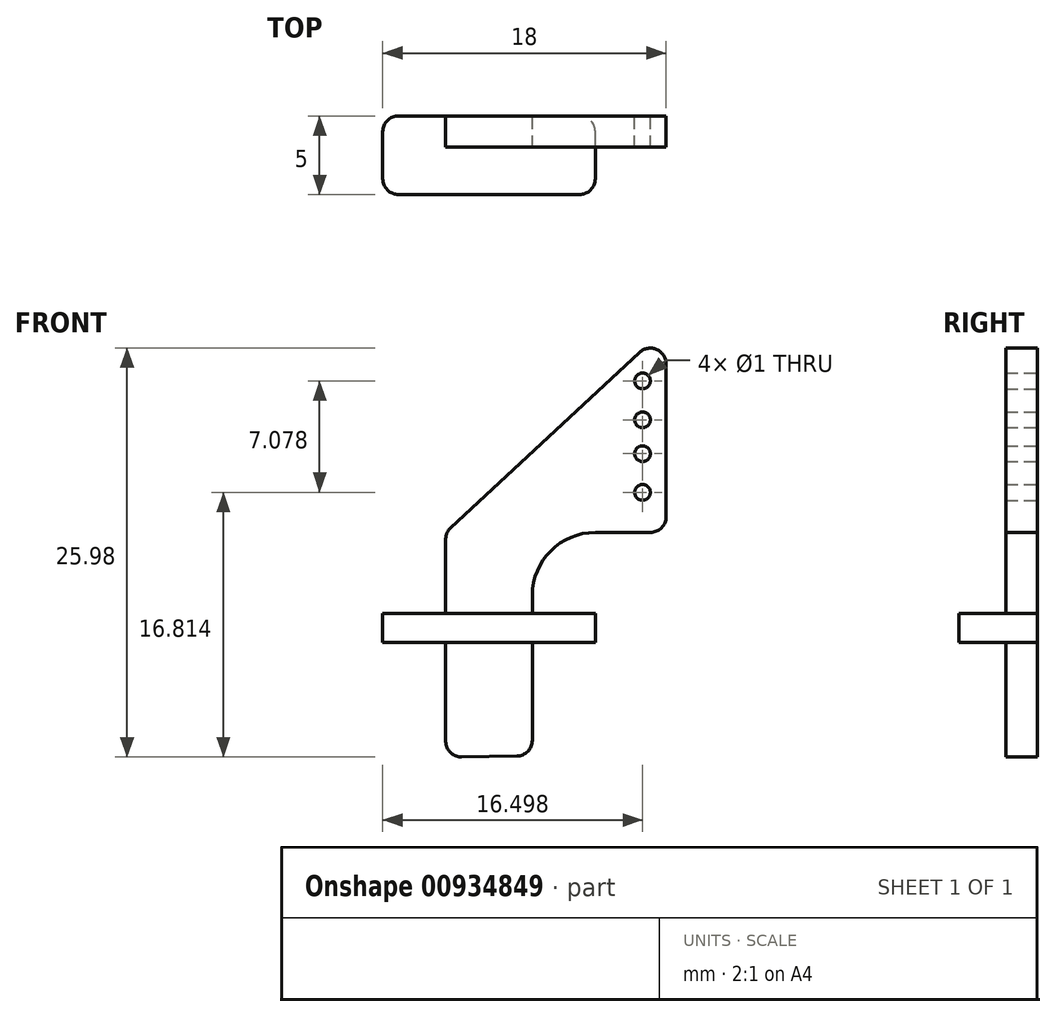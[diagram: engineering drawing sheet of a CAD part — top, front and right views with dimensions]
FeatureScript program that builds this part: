
annotation { "Feature Type Name" : "Feature", "Feature Type Description" : "" }
export const myFeature = defineFeature(function(context is Context, id is Id, definition is map)
    precondition{}
    {
        {
            var Q0;
            Q0=qCreatedBy(makeId("Front.planeOp"),FACE);
            var sketch = newSketch(context, id + "F0", { "sketchPlane" : qUnion([Q0])});
            skLineSegment(sketch, "E0", {"start": v(0, 20.31) * mm, "end": v(0, -7.28) * mm});
            skLineSegment(sketch, "E1", {"start": v(14, 21.92) * mm, "end": v(14, -6.72) * mm});
            skLineSegment(sketch, "E2", {"start": v(-2.14, 7) * mm, "end": v(19.55, 7) * mm});
            skLineSegment(sketch, "E3", {"start": v(-2.78, 20) * mm, "end": v(21.74, 20) * mm});
            skLineSegment(sketch, "E4", {"start": v(0, 7) * mm, "end": v(14, 20) * mm});
            skLineSegment(sketch, "E5", {"start": v(5.5, -7.19) * mm, "end": v(5.5, 24.92) * mm});
            skLineSegment(sketch, "E6", {"start": v(0, -7.28) * mm, "end": v(5.5, -7.19) * mm});
            skSolve(sketch);
        }
        {
            var Q0;
            {var subQ1=sQuery(id+"F0.wireOp",EDGE,"E1");var subQ3=sQuery(id+"F0.wireOp",EDGE,"E2");var subQ4=makeQuery(id+"F0.imprint","INTERSECT",VERTEX,{"derivedFrom":[subQ1,subQ3]});Q0=makeQuery(id+"F0.imprint","IMPRINT",FACE,{"disambiguationData":[TD([[makeQuery(id+"F0.imprint","IMPRINT",EDGE,{"disambiguationData":[TD([[subQ4,1.0]])],"derivedFrom":subQ3}),1.0]])]});}
            var Q1;
            {var subQ1=sQuery(id+"F0.wireOp",EDGE,"E2");var subQ3=sQuery(id+"F0.wireOp",EDGE,"E5");var subQ4=makeQuery(id+"F0.imprint","INTERSECT",VERTEX,{"derivedFrom":[subQ1,subQ3]});Q1=makeQuery(id+"F0.imprint","IMPRINT",FACE,{"disambiguationData":[TD([[makeQuery(id+"F0.imprint","IMPRINT",EDGE,{"disambiguationData":[TD([[subQ4,-1.0]])],"derivedFrom":subQ3}),1.0]])]});}
            var Q2;
            {var subQ0=sQuery(id+"F0.wireOp",EDGE,"E6");Q2=makeQuery(id+"F0.imprint","IMPRINT",FACE,{"disambiguationData":[TD([[makeQuery(id+"F0.imprint","IMPRINT",EDGE,{"derivedFrom":subQ0}),1.0]])]});}
            extrude(context, id + "F1", {"entities" : qUnion([Q0, Q1, Q2]), "depth" : 2 * mm, "offsetDistance" : 25 * mm});
        }
        {
            var Q0;
            Q0=makeQuery(id+"F1.opExtrude","SWEPT_EDGE",EDGE,{"disambiguationData":[OSD([sQuery(id+"F0.wireOp",EDGE,"E0"),sQuery(id+"F0.wireOp",EDGE,"E2"),sQuery(id+"F0.wireOp",EDGE,"E4")])]});
            var Q1;
            Q1=makeQuery(id+"F1.opExtrude","SWEPT_EDGE",EDGE,{"disambiguationData":[OSD([sQuery(id+"F0.wireOp",EDGE,"E1"),sQuery(id+"F0.wireOp",EDGE,"E3"),sQuery(id+"F0.wireOp",EDGE,"E4")])]});
            var Q2;
            Q2=makeQuery(id+"F1.opExtrude","SWEPT_EDGE",EDGE,{"disambiguationData":[OSD([sQuery(id+"F0.wireOp",EDGE,"E1"),sQuery(id+"F0.wireOp",EDGE,"E2")])]});
            var Q3;
            Q3=makeQuery(id+"F1.opExtrude","SWEPT_EDGE",EDGE,{"disambiguationData":[OSD([sQuery(id+"F0.wireOp",EDGE,"E0"),sQuery(id+"F0.wireOp",EDGE,"E6")])]});
            var Q4;
            Q4=makeQuery(id+"F1.opExtrude","SWEPT_EDGE",EDGE,{"disambiguationData":[OSD([sQuery(id+"F0.wireOp",EDGE,"E5"),sQuery(id+"F0.wireOp",EDGE,"E6")])]});
            fillet(context, id + "F2", {"entities" : qUnion([Q0, Q1, Q2, Q3, Q4]), "radius" : 1 * mm, "tangentPropagation" : true, "allowEdgeOverflow" : false});
        }
        {
            var Q0;
            Q0=makeQuery(id+"F1.opExtrude","SWEPT_EDGE",EDGE,{"disambiguationData":[OSD([sQuery(id+"F0.wireOp",EDGE,"E2"),sQuery(id+"F0.wireOp",EDGE,"E5")])]});
            fillet(context, id + "F3", {"entities" : qUnion([Q0]), "radius" : 4 * mm, "tangentPropagation" : true, "allowEdgeOverflow" : false});
        }
        {
            var Q0;
            Q0=qCreatedBy(makeId("Front.planeOp"),FACE);
            var sketch = newSketch(context, id + "F4", { "sketchPlane" : qUnion([Q0])});
            skLineSegment(sketch, "E7", {"start": v(-8.2, 0) * mm, "end": v(19.5, 0) * mm});
            skLineSegment(sketch, "E8", {"start": v(-4, 7.31) * mm, "end": v(-4, -8.29) * mm});
            skLineSegment(sketch, "E9", {"start": v(9.5, 4.3) * mm, "end": v(9.5, -6.98) * mm});
            skLineSegment(sketch, "E10", {"start": v(12.5, 20.9) * mm, "end": v(12.5, 3.1) * mm});
            skPoint(sketch, "E11", {"position": v(12.5, 16.62) * mm});
            skPoint(sketch, "E12", {"position": v(12.5, 14.15) * mm});
            skPoint(sketch, "E13", {"position": v(12.5, 12) * mm});
            skPoint(sketch, "E14", {"position": v(12.5, 9.54) * mm});
            skLineSegment(sketch, "E15.MirrorCS", {"start": v(-7.95, 1.86) * mm, "end": v(20.52, 1.86) * mm});
            skSolve(sketch);
        }
        {
            var Q0;
            {var subQ0=sQuery(id+"F4.wireOp",EDGE,"E8");var subQ1=sQuery(id+"F4.wireOp",EDGE,"E7");var subQ2=makeQuery(id+"F4.imprint","INTERSECT",VERTEX,{"derivedFrom":[subQ1,subQ0]});Q0=makeQuery(id+"F4.imprint","IMPRINT",FACE,{"disambiguationData":[TD([[makeQuery(id+"F4.imprint","IMPRINT",EDGE,{"disambiguationData":[TD([[subQ2,-1.0]])],"derivedFrom":subQ1}),1.0]])]});}
            extrude(context, id + "F5", {"entities" : qUnion([Q0]), "operationType" : NewBodyOperationType.ADD, "depth" : 5 * mm, "offsetDistance" : 25 * mm});
        }
        {
            var Q0;
            Q0=makeQuery(id+"F5.opExtrude","CAP_EDGE",EDGE,{"disambiguationData":[OSD([sQuery(id+"F4.wireOp",EDGE,"E9")])],"isStart":false});
            var Q1;
            Q1=makeQuery(id+"F5.opExtrude","CAP_EDGE",EDGE,{"disambiguationData":[OSD([sQuery(id+"F4.wireOp",EDGE,"E8")])],"isStart":false});
            var Q2;
            Q2=makeQuery(id+"F5.opExtrude","CAP_EDGE",EDGE,{"disambiguationData":[OSD([sQuery(id+"F4.wireOp",EDGE,"E8")])],"isStart":true});
            var Q3;
            Q3=makeQuery(id+"F5.opExtrude","CAP_EDGE",EDGE,{"disambiguationData":[OSD([sQuery(id+"F4.wireOp",EDGE,"E9")])],"isStart":true});
            fillet(context, id + "F6", {"entities" : qUnion([Q0, Q1, Q2, Q3]), "radius" : 1 * mm, "tangentPropagation" : true, "allowEdgeOverflow" : false});
        }
        {
            var Q0;
            Q0=sQuery(id+"F4.wireOp",VERTEX,"E11");
            var Q1;
            Q1=sQuery(id+"F4.wireOp",VERTEX,"E12");
            var Q2;
            Q2=sQuery(id+"F4.wireOp",VERTEX,"E13");
            var Q3;
            Q3=sQuery(id+"F4.wireOp",VERTEX,"E14");
            var Q4;
            Q4=makeQuery(id+"F1.opExtrude","SWEPT_BODY",BODY,{"disambiguationData":[OSD([sQuery(id+"F0.wireOp",EDGE,"E0"),sQuery(id+"F0.wireOp",EDGE,"E1"),sQuery(id+"F0.wireOp",EDGE,"E2"),sQuery(id+"F0.wireOp",EDGE,"E4"),sQuery(id+"F0.wireOp",EDGE,"E5"),sQuery(id+"F0.wireOp",EDGE,"E6")])]});
            hole(context, id + "F7", {"style" : HoleStyle.SIMPLE, "endStyle" : HoleEndStyle.THROUGH, "oppositeDirection" : true, "holeDiameter" : 1 * mm, "majorDiameter" : 5 * mm, "isTappedThrough" : true, "tappedDepth" : 12.7 * mm, "tapClearance" : 3, "startFromSketch" : true, "locations" : qUnion([Q0, Q1, Q2, Q3]), "scope" : qUnion([Q4])});
        }
    });
